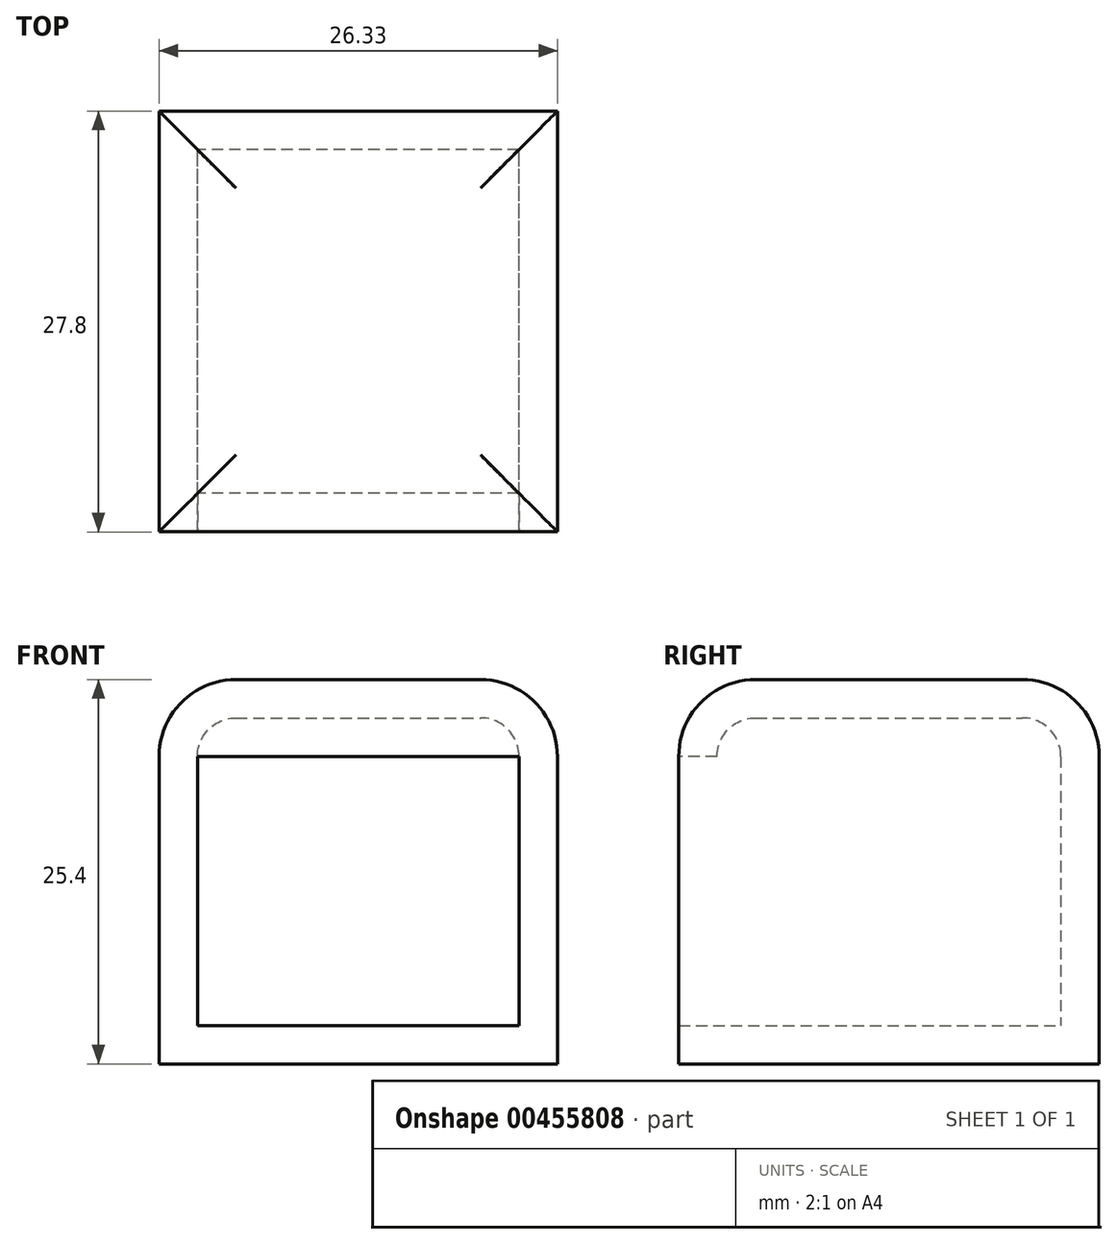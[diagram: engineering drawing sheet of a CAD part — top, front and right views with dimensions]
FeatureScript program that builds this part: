
annotation { "Feature Type Name" : "Feature", "Feature Type Description" : "" }
export const myFeature = defineFeature(function(context is Context, id is Id, definition is map)
    precondition{}
    {
        {
            var Q0;
            Q0=qCreatedBy(makeId("Top.planeOp"),FACE);
            var sketch = newSketch(context, id + "F0", { "sketchPlane" : qUnion([Q0])});
            skLineSegment(sketch, "E0.bottom", {"start": v(0, -0.76) * mm, "end": v(-26.33, -0.76) * mm});
            skLineSegment(sketch, "E0.top", {"start": v(0, 27.04) * mm, "end": v(-26.33, 27.04) * mm});
            skLineSegment(sketch, "E0.left", {"start": v(0, -0.76) * mm, "end": v(0, 27.04) * mm});
            skLineSegment(sketch, "E0.right", {"start": v(-26.33, -0.76) * mm, "end": v(-26.33, 27.04) * mm});
            skSolve(sketch);
        }
        {
            var Q0;
            Q0 = qSketchRegion(id + "F0", true);
            extrude(context, id + "F1", {"entities" : qUnion([Q0]), "depth" : 25.4 * mm});
        }
        {
            var Q0;
            Q0=makeQuery(id+"F1.opExtrude","CAP_EDGE",EDGE,{"disambiguationData":[OSD([sQuery(id+"F0.wireOp",EDGE,"E0.right")])],"isStart":false});
            var Q1;
            Q1=makeQuery(id+"F1.opExtrude","CAP_EDGE",EDGE,{"disambiguationData":[OSD([sQuery(id+"F0.wireOp",EDGE,"E0.bottom")])],"isStart":false});
            var Q2;
            Q2=makeQuery(id+"F1.opExtrude","CAP_EDGE",EDGE,{"disambiguationData":[OSD([sQuery(id+"F0.wireOp",EDGE,"E0.left")])],"isStart":false});
            var Q3;
            Q3=makeQuery(id+"F1.opExtrude","CAP_EDGE",EDGE,{"disambiguationData":[OSD([sQuery(id+"F0.wireOp",EDGE,"E0.top")])],"isStart":false});
            fillet(context, id + "F2", {"entities" : qUnion([Q0, Q1, Q2, Q3]), "radius" : 5.08 * mm, "tangentPropagation" : true, "allowEdgeOverflow" : false});
        }
        {
            var Q0;
            Q0=makeQuery(id+"F1.opExtrude","SWEPT_FACE",FACE,{"disambiguationData":[OSD([sQuery(id+"F0.wireOp",EDGE,"E0.bottom")])]});
            shell(context, id + "F3", {"entities" : qUnion([Q0]), "thickness" : 2.54 * mm});
        }
    });
